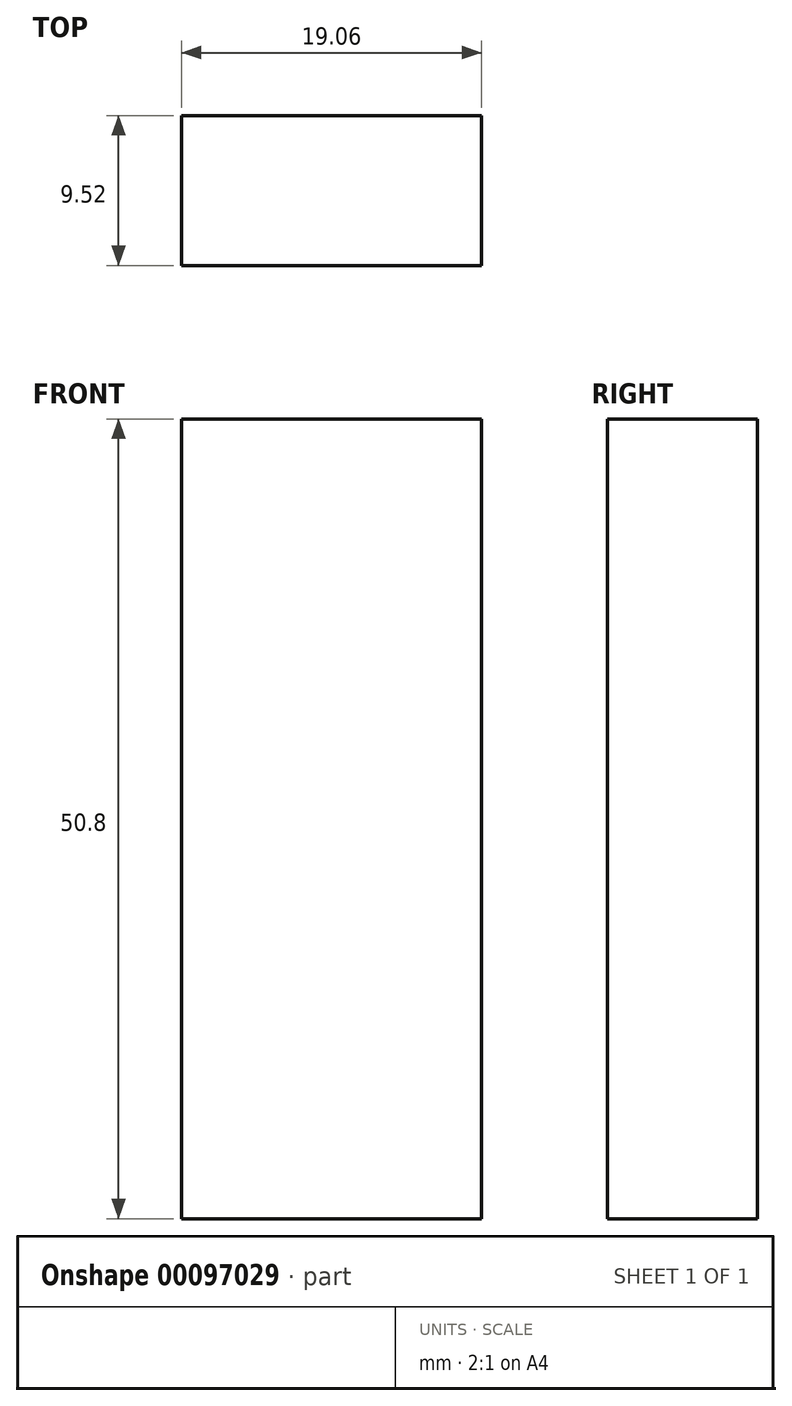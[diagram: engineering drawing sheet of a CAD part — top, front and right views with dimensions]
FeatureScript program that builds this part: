
annotation { "Feature Type Name" : "Feature", "Feature Type Description" : "" }
export const myFeature = defineFeature(function(context is Context, id is Id, definition is map)
    precondition{}
    {
        {
            var Q0;
            Q0=qCreatedBy(makeId("Front.planeOp"),FACE);
            var sketch = newSketch(context, id + "F0", { "sketchPlane" : qUnion([Q0])});
            skLineSegment(sketch, "E0.bottom", {"start": v(9.53, 25.4) * mm, "end": v(-9.53, 25.4) * mm});
            skLineSegment(sketch, "E0.top", {"start": v(9.53, -25.4) * mm, "end": v(-9.53, -25.4) * mm});
            skLineSegment(sketch, "E0.left", {"start": v(9.53, 25.4) * mm, "end": v(9.53, -25.4) * mm});
            skLineSegment(sketch, "E0.right", {"start": v(-9.53, 25.4) * mm, "end": v(-9.53, -25.4) * mm});
            skPoint(sketch, "E0.middle", {"position": v(0, 0) * mm});
            skSolve(sketch);
        }
        {
            var Q0;
            Q0 = qSketchRegion(id + "F0", true);
            extrude(context, id + "F1", {"entities" : qUnion([Q0]), "endBound" : BoundingType.SYMMETRIC, "depth" : 9.52 * mm});
        }
    });
